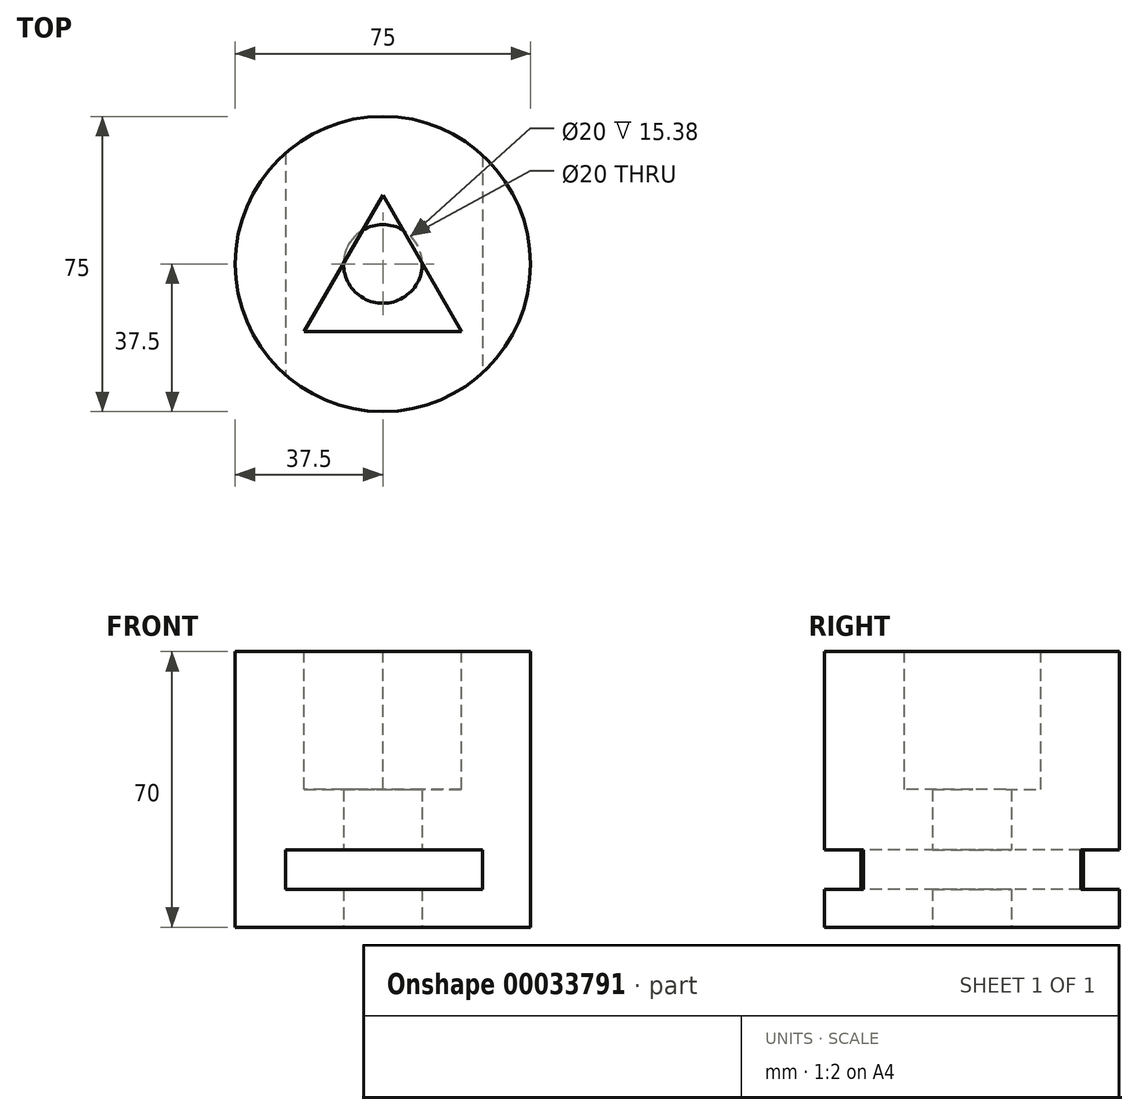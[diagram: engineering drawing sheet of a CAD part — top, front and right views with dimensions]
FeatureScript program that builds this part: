
annotation { "Feature Type Name" : "Feature", "Feature Type Description" : "" }
export const myFeature = defineFeature(function(context is Context, id is Id, definition is map)
    precondition{}
    {
        {
            var Q0;
            Q0=qCreatedBy(makeId("Top.planeOp"),FACE);
            var sketch = newSketch(context, id + "F0", { "sketchPlane" : qUnion([Q0])});
            skCircle(sketch, "E0", {"center": v(0, 0) * mm, "radius": 37.5 * mm});
            skSolve(sketch);
        }
        {
            var Q0;
            Q0=makeQuery(id+"F0.imprint","IMPRINT",FACE,{"disambiguationData":[TD([[makeQuery(id+"F0.imprint","IMPRINT",EDGE,{"derivedFrom":sQuery(id+"F0.wireOp",EDGE,"E0")}),1.0]])]});
            extrude(context, id + "F1", {"entities" : qUnion([Q0]), "depth" : 70 * mm});
        }
        {
            var Q0;
            Q0=makeQuery(id+"F1.opExtrude","CAP_FACE",FACE,{"disambiguationData":[OSD([sQuery(id+"F0.wireOp",EDGE,"E0")])],"isStart":true});
            var sketch = newSketch(context, id + "F2", { "sketchPlane" : qUnion([Q0])});
            skCircle(sketch, "E1", {"center": v(0, 0) * mm, "radius": 10 * mm});
            skSolve(sketch);
        }
        {
            var Q0;
            Q0=makeQuery(id+"F2.imprint","IMPRINT",FACE,{"disambiguationData":[TD([[makeQuery(id+"F2.imprint","IMPRINT",EDGE,{"derivedFrom":sQuery(id+"F2.wireOp",EDGE,"E1")}),1.0]])]});
            extrude(context, id + "F3", {"entities" : qUnion([Q0]), "operationType" : NewBodyOperationType.REMOVE, "oppositeDirection" : true, "depth" : 35 * mm});
        }
        {
            var Q0;
            Q0=makeQuery(id+"F1.opExtrude","CAP_FACE",FACE,{"disambiguationData":[OSD([sQuery(id+"F0.wireOp",EDGE,"E0")])],"isStart":false});
            var sketch = newSketch(context, id + "F4", { "sketchPlane" : qUnion([Q0])});
            skLineSegment(sketch, "E2", {"start": v(-20, -17.14) * mm, "end": v(20, -17.14) * mm});
            skLineSegment(sketch, "E3", {"start": v(20, -17.14) * mm, "end": v(0, 17.5) * mm});
            skLineSegment(sketch, "E4", {"start": v(0, 17.5) * mm, "end": v(-20, -17.14) * mm});
            skSolve(sketch);
        }
        {
            var Q0;
            Q0=makeQuery(id+"F4.imprint","IMPRINT",FACE,{"disambiguationData":[TD([[makeQuery(id+"F4.imprint","IMPRINT",EDGE,{"derivedFrom":sQuery(id+"F4.wireOp",EDGE,"E2")}),1.0]])]});
            extrude(context, id + "F5", {"entities" : qUnion([Q0]), "operationType" : NewBodyOperationType.REMOVE, "oppositeDirection" : true, "depth" : 35 * mm});
        }
        {
            var Q0;
            Q0=qCreatedBy(makeId("Front.planeOp"),FACE);
            var sketch = newSketch(context, id + "F7", { "sketchPlane" : qUnion([Q0])});
            skLineSegment(sketch, "E5.bottom", {"start": v(-24.67, 19.62) * mm, "end": v(25.33, 19.62) * mm});
            skLineSegment(sketch, "E5.top", {"start": v(-24.67, 9.62) * mm, "end": v(25.33, 9.62) * mm});
            skLineSegment(sketch, "E5.left", {"start": v(-24.67, 19.62) * mm, "end": v(-24.67, 9.62) * mm});
            skLineSegment(sketch, "E5.right", {"start": v(25.33, 19.62) * mm, "end": v(25.33, 9.62) * mm});
            skSolve(sketch);
        }
        {
            var Q0;
            Q0=makeQuery(id+"F7.imprint","IMPRINT",FACE,{"disambiguationData":[TD([[makeQuery(id+"F7.imprint","IMPRINT",EDGE,{"derivedFrom":sQuery(id+"F7.wireOp",EDGE,"E5.bottom")}),-1.0]])]});
            extrude(context, id + "F6", {"entities" : qUnion([Q0]), "operationType" : NewBodyOperationType.REMOVE, "endBound" : BoundingType.SYMMETRIC, "oppositeDirection" : true, "depth" : 80 * mm});
        }
    });
